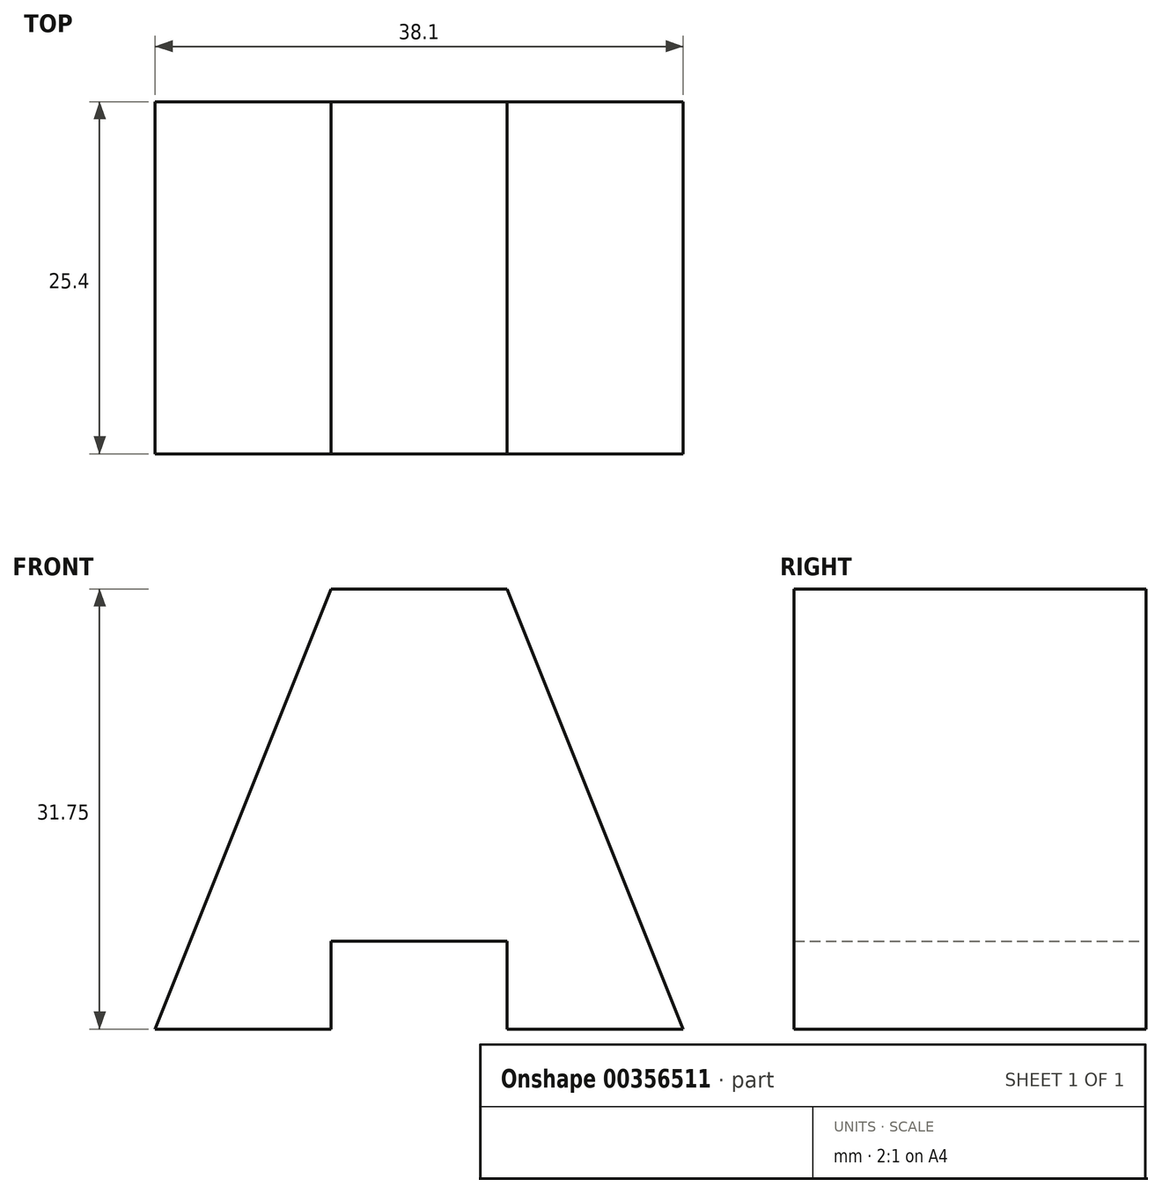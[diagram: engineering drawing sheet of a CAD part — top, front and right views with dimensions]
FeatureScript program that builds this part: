
annotation { "Feature Type Name" : "Feature", "Feature Type Description" : "" }
export const myFeature = defineFeature(function(context is Context, id is Id, definition is map)
    precondition{}
    {
        {
            var Q0;
            Q0=qCreatedBy(makeId("Front.planeOp"),FACE);
            var sketch = newSketch(context, id + "F0", { "sketchPlane" : qUnion([Q0])});
            skLineSegment(sketch, "E0", {"start": v(0, 0) * mm, "end": v(12.7, 31.75) * mm});
            skLineSegment(sketch, "E1", {"start": v(12.7, 31.75) * mm, "end": v(25.4, 31.75) * mm});
            skLineSegment(sketch, "E2", {"start": v(25.4, 31.75) * mm, "end": v(38.1, 0) * mm});
            skLineSegment(sketch, "E3", {"start": v(38.1, 0) * mm, "end": v(25.4, 0) * mm});
            skLineSegment(sketch, "E4", {"start": v(25.4, 0) * mm, "end": v(25.4, 6.35) * mm});
            skLineSegment(sketch, "E5", {"start": v(25.4, 6.35) * mm, "end": v(12.7, 6.35) * mm});
            skLineSegment(sketch, "E6", {"start": v(12.7, 6.35) * mm, "end": v(12.7, 0) * mm});
            skLineSegment(sketch, "E7", {"start": v(12.7, 0) * mm, "end": v(0, 0) * mm});
            skSolve(sketch);
        }
        {
            var Q0;
            Q0 = qSketchRegion(id + "F0", true);
            extrude(context, id + "F1", {"entities" : qUnion([Q0]), "depth" : 25.4 * mm});
        }
    });
